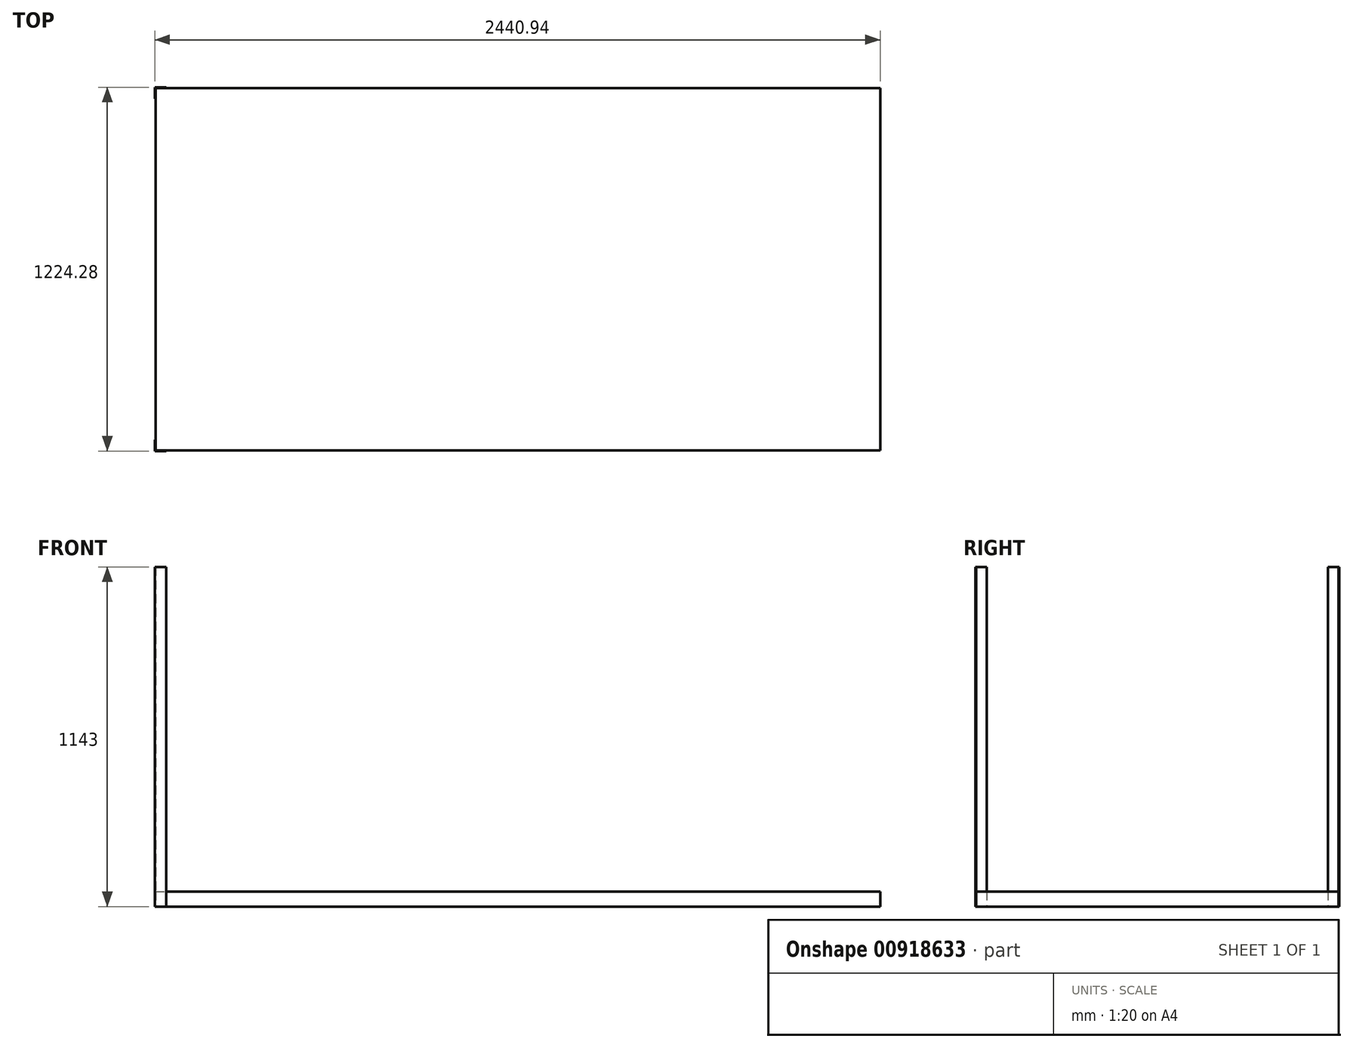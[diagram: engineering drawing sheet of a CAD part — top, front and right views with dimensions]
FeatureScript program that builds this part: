
annotation { "Feature Type Name" : "Feature", "Feature Type Description" : "" }
export const myFeature = defineFeature(function(context is Context, id is Id, definition is map)
    precondition{}
    {
        {
            var Q0;
            Q0=qCreatedBy(makeId("Top.planeOp"),FACE);
            var sketch = newSketch(context, id + "F0", { "sketchPlane" : qUnion([Q0])});
            skLineSegment(sketch, "E0.bottom", {"start": v(-1219.2, 609.6) * mm, "end": v(1219.2, 609.6) * mm});
            skLineSegment(sketch, "E0.top", {"start": v(-1219.2, -609.6) * mm, "end": v(1219.2, -609.6) * mm});
            skLineSegment(sketch, "E0.left", {"start": v(-1219.2, 609.6) * mm, "end": v(-1219.2, -609.6) * mm});
            skLineSegment(sketch, "E0.right", {"start": v(1219.2, 609.6) * mm, "end": v(1219.2, -609.6) * mm});
            skLineSegment(sketch, "E1", {"start": v(-1219.2, 609.6) * mm, "end": v(1219.2, -609.6) * mm, "construction": true});
            skSolve(sketch);
        }
        {
            var Q0;
            Q0 = qSketchRegion(id + "F0", true);
            extrude(context, id + "F1", {"entities" : qUnion([Q0]), "depth" : 50.8 * mm, "offsetDistance" : 25.4 * mm});
        }
        {
            var Q0;
            Q0=makeQuery(id+"F1.opExtrude","CAP_FACE",FACE,{"disambiguationData":[OSD([sQuery(id+"F0.wireOp",EDGE,"E0.bottom"),sQuery(id+"F0.wireOp",EDGE,"E0.top"),sQuery(id+"F0.wireOp",EDGE,"E0.left"),sQuery(id+"F0.wireOp",EDGE,"E0.right")])],"isStart":true});
            var sketch = newSketch(context, id + "F2", { "sketchPlane" : qUnion([Q0])});
            skLineSegment(sketch, "E2", {"start": v(-1221.74, 612.14) * mm, "end": v(-1221.74, 574.04) * mm});
            skLineSegment(sketch, "E3", {"start": v(-1221.74, 574.04) * mm, "end": v(-1219.2, 574.04) * mm});
            skLineSegment(sketch, "E4", {"start": v(-1219.2, 574.04) * mm, "end": v(-1219.2, 609.6) * mm});
            skLineSegment(sketch, "E5", {"start": v(-1219.2, 609.6) * mm, "end": v(-1183.64, 609.6) * mm});
            skLineSegment(sketch, "E6", {"start": v(-1183.64, 609.6) * mm, "end": v(-1183.64, 612.14) * mm});
            skLineSegment(sketch, "E7", {"start": v(-1183.64, 612.14) * mm, "end": v(-1221.74, 612.14) * mm});
            skSolve(sketch);
        }
        {
            var Q0;
            Q0=makeQuery(id+"F2.imprint","IMPRINT",FACE,{"disambiguationData":[TD([[makeQuery(id+"F2.imprint","IMPRINT",EDGE,{"derivedFrom":sQuery(id+"F2.wireOp",EDGE,"E2")}),1.0]])]});
            extrude(context, id + "F3", {"entities" : qUnion([Q0]), "operationType" : NewBodyOperationType.ADD, "oppositeDirection" : true, "depth" : 1143 * mm, "offsetDistance" : 25.4 * mm});
        }
        {
            var Q0;
            Q0=makeQuery(id+"F1.opExtrude","SWEPT_BODY",BODY,{"disambiguationData":[OSD([sQuery(id+"F0.wireOp",EDGE,"E0.bottom"),sQuery(id+"F0.wireOp",EDGE,"E0.top"),sQuery(id+"F0.wireOp",EDGE,"E0.left"),sQuery(id+"F0.wireOp",EDGE,"E0.right")])]});
            var Q1;
            Q1=qCreatedBy(makeId("Front.planeOp"),FACE);
            mirror(context, id + "F4", {"operationType" : NewBodyOperationType.ADD, "entities" : qUnion([Q0]), "mirrorPlane" : qUnion([Q1])});
        }
    });
